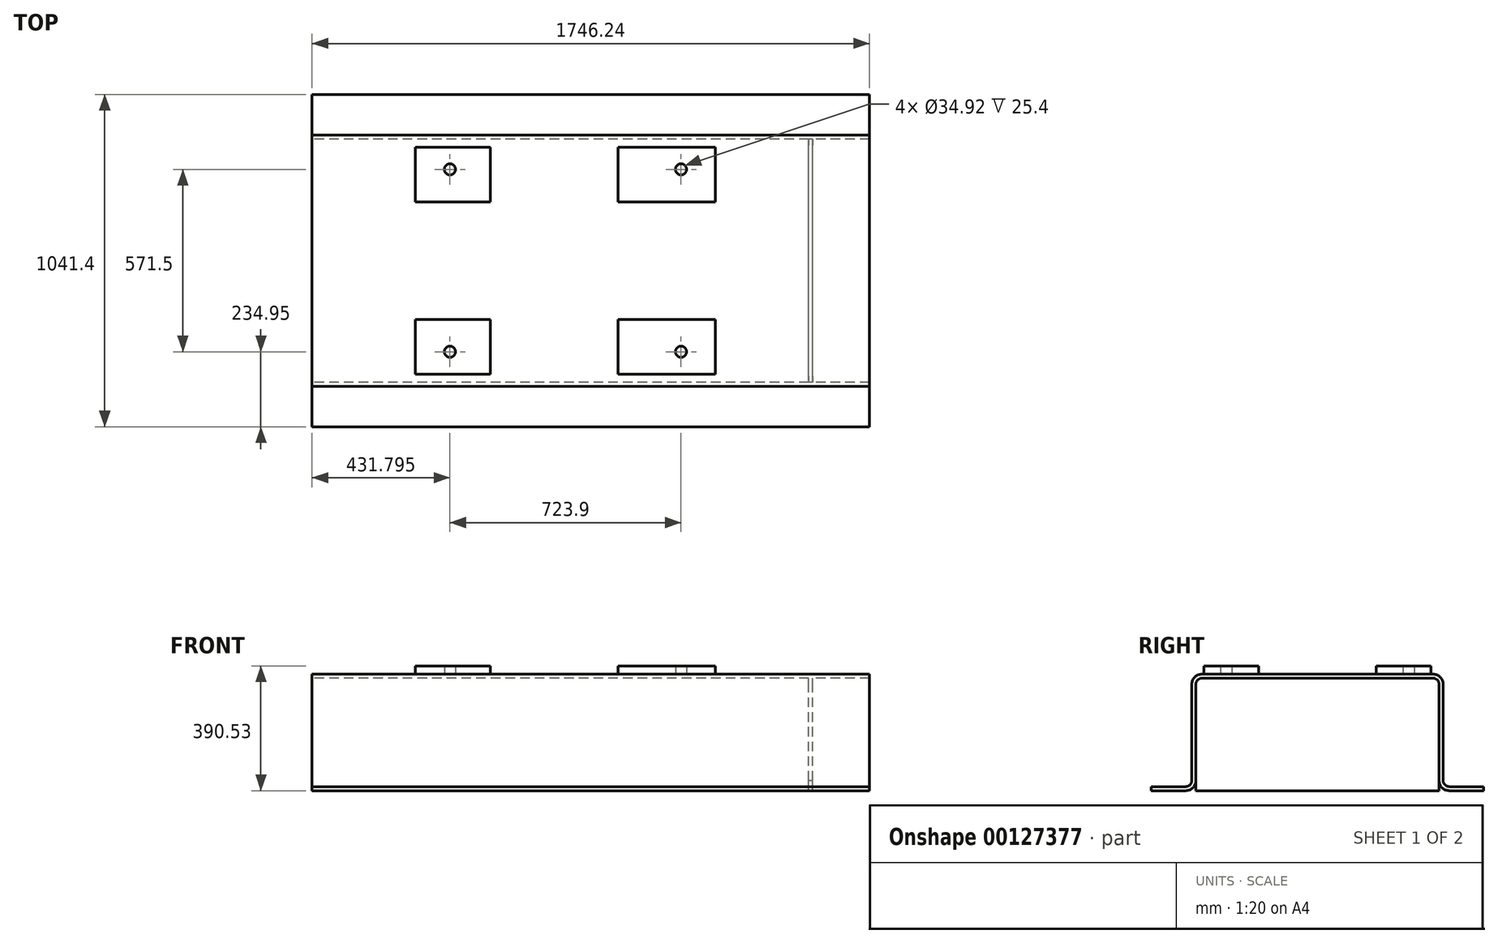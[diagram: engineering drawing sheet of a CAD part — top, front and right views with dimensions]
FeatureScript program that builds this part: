
annotation { "Feature Type Name" : "Feature", "Feature Type Description" : "" }
export const myFeature = defineFeature(function(context is Context, id is Id, definition is map)
    precondition{}
    {
        {
            var Q0;
            Q0=qCreatedBy(makeId("Right.planeOp"),FACE);
            var sketch = newSketch(context, id + "F0", { "sketchPlane" : qUnion([Q0])});
            skLineSegment(sketch, "E0", {"start": v(412.75, 0) * mm, "end": v(520.7, 0) * mm});
            skLineSegment(sketch, "E1.0", {"start": v(0, 365.13) * mm, "end": v(361.95, 365.13) * mm});
            skLineSegment(sketch, "E2", {"start": v(0, -73.94) * mm, "end": v(0, 485.88) * mm, "construction": true});
            skLineSegment(sketch, "E3.0", {"start": v(412.75, 12.7) * mm, "end": v(520.7, 12.7) * mm});
            skLineSegment(sketch, "E4.0", {"start": v(0, 352.43) * mm, "end": v(361.95, 352.43) * mm});
            skLineSegment(sketch, "E5.0", {"start": v(393.7, 31.75) * mm, "end": v(393.7, 333.38) * mm});
            skLineSegment(sketch, "E6.0", {"start": v(381, 31.75) * mm, "end": v(381, 333.38) * mm});
            skArc(sketch, "E7.filletArc", {"start": v(381, 333.38) * mm, "mid": v(375.42, 346.85) * mm, "end": v(361.95, 352.43) * mm});
            skArc(sketch, "E8.filletArc", {"start": v(393.7, 31.75) * mm, "mid": v(399.28, 18.28) * mm, "end": v(412.75, 12.7) * mm});
            skArc(sketch, "E9.filletArc", {"start": v(393.7, 333.38) * mm, "mid": v(384.4, 355.83) * mm, "end": v(361.95, 365.13) * mm});
            skPoint(sketch, "E10.newPointB", {"position": v(-520.7, 0) * mm});
            skArc(sketch, "E10.filletArc", {"start": v(381, 31.75) * mm, "mid": v(390.3, 9.3) * mm, "end": v(412.75, 0) * mm});
            skLineSegment(sketch, "E11", {"start": v(520.7, 12.7) * mm, "end": v(520.7, 0) * mm});
            skLineSegment(sketch, "E12.MirrorCS", {"start": v(-520.7, 12.7) * mm, "end": v(-520.7, 0) * mm});
            skArc(sketch, "E13.MirrorCS", {"start": v(-381, 333.38) * mm, "mid": v(-375.42, 346.85) * mm, "end": v(-361.95, 352.43) * mm});
            skArc(sketch, "E14.MirrorCS", {"start": v(-393.7, 31.75) * mm, "mid": v(-399.28, 18.28) * mm, "end": v(-412.75, 12.7) * mm});
            skArc(sketch, "E15.MirrorCS", {"start": v(-381, 31.75) * mm, "mid": v(-390.3, 9.3) * mm, "end": v(-412.75, 0) * mm});
            skLineSegment(sketch, "E16.MirrorCS", {"start": v(-412.75, 0) * mm, "end": v(-520.7, 0) * mm});
            skLineSegment(sketch, "E17.MirrorCS", {"start": v(0, 365.13) * mm, "end": v(-361.95, 365.13) * mm});
            skLineSegment(sketch, "E18.MirrorCS", {"start": v(-412.75, 12.7) * mm, "end": v(-520.7, 12.7) * mm});
            skLineSegment(sketch, "E19.MirrorCS", {"start": v(-381, 31.75) * mm, "end": v(-381, 333.38) * mm});
            skArc(sketch, "E20.MirrorCS", {"start": v(-393.7, 333.38) * mm, "mid": v(-384.4, 355.83) * mm, "end": v(-361.95, 365.13) * mm});
            skLineSegment(sketch, "E21.MirrorCS", {"start": v(0, 352.43) * mm, "end": v(-361.95, 352.43) * mm});
            skLineSegment(sketch, "E22.MirrorCS", {"start": v(-393.7, 31.75) * mm, "end": v(-393.7, 333.38) * mm});
            skSolve(sketch);
        }
        {
            var Q0;
            Q0=qSketchRegion(id+"F0",true);
            extrude(context, id + "F1", {"entities" : qUnion([Q0]), "endBound" : BoundingType.SYMMETRIC, "depth" : 1746.25 * mm});
        }
        {
            var Q0;
            Q0=makeQuery(id+"F1.opExtrude","SWEPT_FACE",FACE,{"disambiguationData":[OSD([sQuery(id+"F0.wireOp",EDGE,"E1.0"),sQuery(id+"F0.wireOp",EDGE,"E17.MirrorCS")])]});
            var sketch = newSketch(context, id + "F2", { "sketchPlane" : qUnion([Q0])});
            skLineSegment(sketch, "E23.0", {"start": v(873.12, -361.95) * mm, "end": v(873.12, 361.95) * mm, "construction": true});
            skLineSegment(sketch, "E24.0", {"start": v(644.52, -361.95) * mm, "end": v(644.52, 361.95) * mm, "construction": true});
            skLineSegment(sketch, "E25.0", {"start": v(-79.38, -361.95) * mm, "end": v(-79.38, 361.95) * mm, "construction": true});
            skLineSegment(sketch, "E26.0", {"start": v(390.52, 184.15) * mm, "end": v(390.52, 355.6) * mm});
            skLineSegment(sketch, "E27", {"start": v(-977.5, 0) * mm, "end": v(952.25, 0) * mm, "construction": true});
            skLineSegment(sketch, "E28.0", {"start": v(-549.28, 184.15) * mm, "end": v(-314.33, 184.15) * mm});
            skLineSegment(sketch, "E29.0", {"start": v(-549.28, 355.6) * mm, "end": v(-314.33, 355.6) * mm});
            skLineSegment(sketch, "E30.trimOffspring", {"start": v(-549.28, 184.15) * mm, "end": v(-549.28, 355.6) * mm});
            skLineSegment(sketch, "E31.trimOffspring", {"start": v(85.72, 184.15) * mm, "end": v(390.52, 184.15) * mm});
            skLineSegment(sketch, "E32.trimOffspring", {"start": v(85.72, 355.6) * mm, "end": v(390.52, 355.6) * mm});
            skLineSegment(sketch, "E33.trimOffspring", {"start": v(-314.33, 184.15) * mm, "end": v(-314.33, 355.6) * mm});
            skLineSegment(sketch, "E34.trimOffspring", {"start": v(85.72, 184.15) * mm, "end": v(85.72, 355.6) * mm});
            skLineSegment(sketch, "E35.0", {"start": v(-441.33, -361.95) * mm, "end": v(-441.33, 361.95) * mm, "construction": true});
            skLineSegment(sketch, "E36.0", {"start": v(-977.5, 285.75) * mm, "end": v(952.25, 285.75) * mm, "construction": true});
            skCircle(sketch, "E37", {"center": v(-441.33, 285.75) * mm, "radius": 17.46 * mm});
            skCircle(sketch, "E38.MirrorC", {"center": v(282.57, 285.75) * mm, "radius": 17.46 * mm});
            skLineSegment(sketch, "E39.MirrorCS", {"start": v(85.72, -355.6) * mm, "end": v(390.52, -355.6) * mm});
            skLineSegment(sketch, "E40.MirrorCS", {"start": v(-549.28, -355.6) * mm, "end": v(-314.33, -355.6) * mm});
            skLineSegment(sketch, "E41.MirrorCS", {"start": v(-549.28, -184.15) * mm, "end": v(-549.28, -355.6) * mm});
            skLineSegment(sketch, "E42.MirrorCS", {"start": v(-549.28, -184.15) * mm, "end": v(-314.33, -184.15) * mm});
            skLineSegment(sketch, "E43.MirrorCS", {"start": v(390.52, -184.15) * mm, "end": v(390.52, -355.6) * mm});
            skLineSegment(sketch, "E44.MirrorCS", {"start": v(85.72, -184.15) * mm, "end": v(85.72, -355.6) * mm});
            skCircle(sketch, "E45.MirrorC", {"center": v(282.57, -285.75) * mm, "radius": 17.46 * mm});
            skLineSegment(sketch, "E46.MirrorCS", {"start": v(-314.33, -184.15) * mm, "end": v(-314.33, -355.6) * mm});
            skCircle(sketch, "E47.MirrorC", {"center": v(-441.33, -285.75) * mm, "radius": 17.46 * mm});
            skLineSegment(sketch, "E48.MirrorCS", {"start": v(85.72, -184.15) * mm, "end": v(390.52, -184.15) * mm});
            skSolve(sketch);
        }
        {
            var Q0;
            Q0=qSketchRegion(id+"F2",true);
            extrude(context, id + "F3", {"entities" : qUnion([Q0]), "operationType" : NewBodyOperationType.ADD, "depth" : 25.4 * mm});
        }
        {
            var Q0;
            Q0=makeQuery(id+"F1.opExtrude","SWEPT_FACE",FACE,{"disambiguationData":[OSD([sQuery(id+"F0.wireOp",EDGE,"E4.0"),sQuery(id+"F0.wireOp",EDGE,"E21.MirrorCS")])]});
            var sketch = newSketch(context, id + "F4", { "sketchPlane" : qUnion([Q0])});
            skLineSegment(sketch, "E49.0", {"start": v(873.12, -361.95) * mm, "end": v(873.12, 361.95) * mm, "construction": true});
            skLineSegment(sketch, "E50.0", {"start": v(695.32, -381) * mm, "end": v(695.32, 381) * mm, "construction": true});
            skLineSegment(sketch, "E51.0.1", {"start": v(-873.12, 381) * mm, "end": v(873.12, 381) * mm});
            skLineSegment(sketch, "E51.0.3", {"start": v(873.12, 381) * mm, "end": v(-873.12, 381) * mm});
            skLineSegment(sketch, "E52.0.1", {"start": v(-873.12, -381) * mm, "end": v(873.12, -381) * mm});
            skLineSegment(sketch, "E52.0.3", {"start": v(873.12, -381) * mm, "end": v(-873.12, -381) * mm});
            skLineSegment(sketch, "E53.bottom", {"start": v(695.32, 381) * mm, "end": v(682.62, 381) * mm});
            skLineSegment(sketch, "E53.top", {"start": v(695.32, -381) * mm, "end": v(682.62, -381) * mm});
            skLineSegment(sketch, "E53.left", {"start": v(695.32, 381) * mm, "end": v(695.32, -381) * mm});
            skLineSegment(sketch, "E53.right", {"start": v(682.62, 381) * mm, "end": v(682.62, -381) * mm});
            skSolve(sketch);
        }
        {
            var Q0;
            Q0=qSketchRegion(id+"F4",true);
            var Q1;
            Q1=makeQuery(id+"F1.opExtrude","SWEPT_FACE",FACE,{"disambiguationData":[OSD([sQuery(id+"F0.wireOp",EDGE,"E16.MirrorCS")])]});
            extrude(context, id + "F5", {"entities" : qUnion([Q0]), "operationType" : NewBodyOperationType.ADD, "endBound" : BoundingType.UP_TO_SURFACE, "endBoundEntityFace" : qUnion([Q1]), "depth" : 25.4 * mm});
        }
    });
